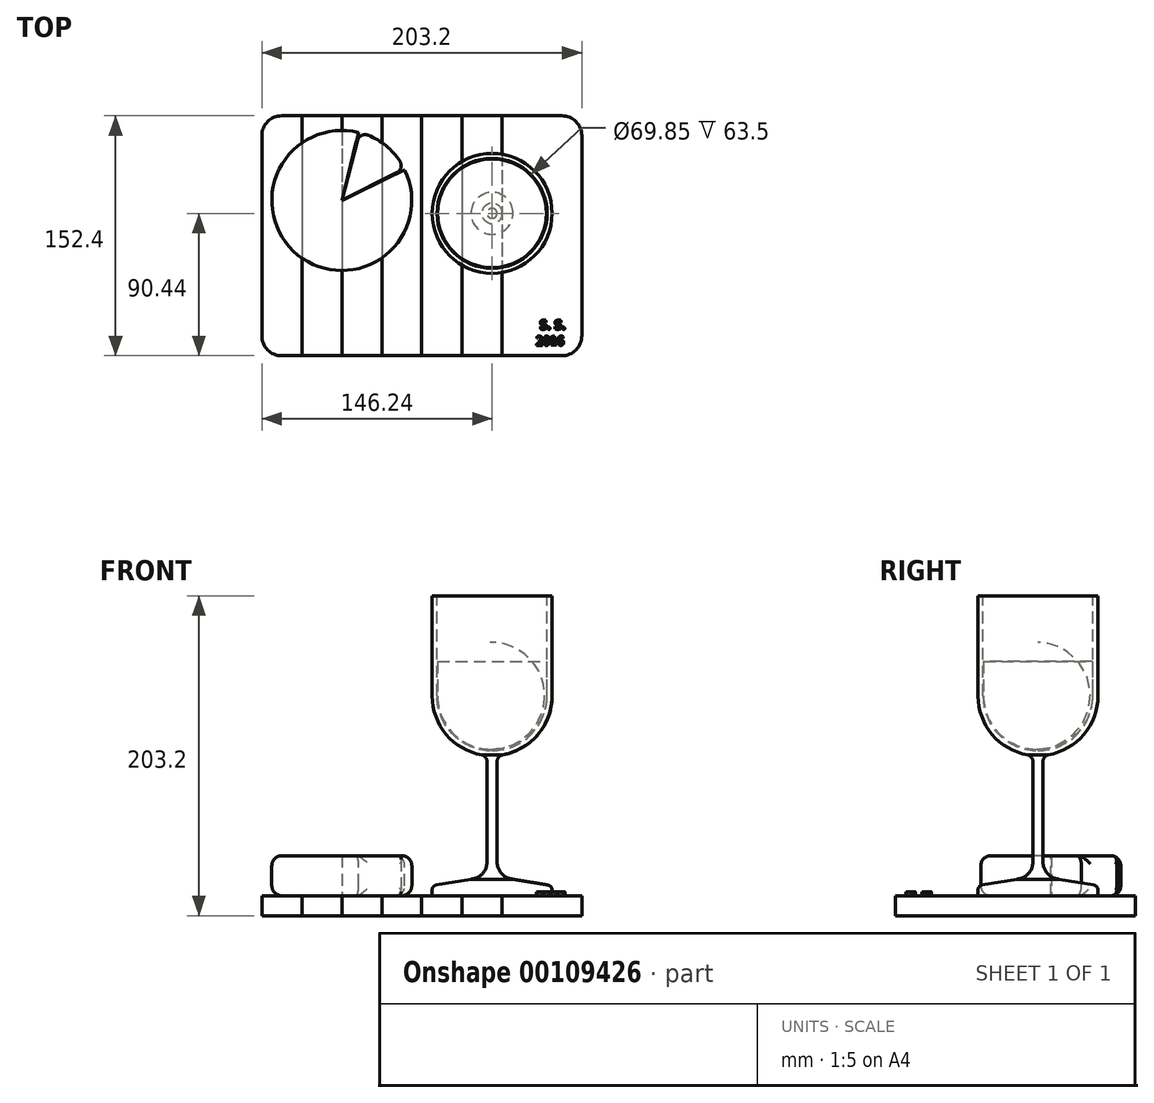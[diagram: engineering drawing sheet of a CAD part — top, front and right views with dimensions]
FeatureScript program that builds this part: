
annotation { "Feature Type Name" : "Feature", "Feature Type Description" : "" }
export const myFeature = defineFeature(function(context is Context, id is Id, definition is map)
    precondition{}
    {
        {
            var Q0;
            Q0=qCreatedBy(makeId("Front.planeOp"),FACE);
            var sketch = newSketch(context, id + "F0", { "sketchPlane" : qUnion([Q0])});
            skLineSegment(sketch, "E0", {"start": v(0, 209.71) * mm, "end": v(0, -15.34) * mm, "construction": true});
            skLineSegment(sketch, "E1", {"start": v(0, 0) * mm, "end": v(-38.1, 0) * mm});
            skLineSegment(sketch, "E2", {"start": v(-38.1, 0) * mm, "end": v(-38.1, 3.66) * mm});
            skLineSegment(sketch, "E3", {"start": v(-35.45, 6.8) * mm, "end": v(-13.34, 10.48) * mm});
            skLineSegment(sketch, "E4", {"start": v(0, 12.7) * mm, "end": v(0, 0) * mm});
            skLineSegment(sketch, "E5", {"start": v(-38.1, 190.5) * mm, "end": v(-38.1, 127) * mm});
            skArc(sketch, "E6", {"start": v(-38.1, 127) * mm, "mid": v(-29.14, 102.46) * mm, "end": v(-6.48, 89.46) * mm});
            skPoint(sketch, "E7.visualSharp", {"position": v(-38.1, 6.35) * mm});
            skArc(sketch, "E7.filletArc", {"start": v(-35.45, 6.8) * mm, "mid": v(-37.35, 5.71) * mm, "end": v(-38.1, 3.66) * mm});
            skArc(sketch, "E8.0", {"start": v(-34.92, 127) * mm, "mid": v(-24.7, 102.3) * mm, "end": v(0, 92.07) * mm});
            skLineSegment(sketch, "E8.1", {"start": v(-34.92, 190.5) * mm, "end": v(-34.92, 127) * mm});
            skLineSegment(sketch, "E9", {"start": v(-38.1, 190.5) * mm, "end": v(-34.92, 190.5) * mm});
            skLineSegment(sketch, "E10", {"start": v(0, 88.9) * mm, "end": v(0, 92.07) * mm});
            skLineSegment(sketch, "E11", {"start": v(0, 12.7) * mm, "end": v(0, 88.9) * mm});
            skLineSegment(sketch, "E12", {"start": v(-3.17, 85.1) * mm, "end": v(-3.17, 21.6) * mm});
            skArc(sketch, "E13", {"start": v(-3.17, 85.1) * mm, "mid": v(-4.1, 87.83) * mm, "end": v(-6.48, 89.46) * mm});
            skArc(sketch, "E14", {"start": v(-3.17, 21.6) * mm, "mid": v(-6.1, 14.06) * mm, "end": v(-13.34, 10.48) * mm});
            skSolve(sketch);
        }
        {
            var Q0;
            Q0 = qSketchRegion(id + "F0", true);
            var Q1;
            Q1=sQuery(id+"F0.wireOp",EDGE,"E0");
            revolve(context, id + "F1", {"entities" : qUnion([Q0]), "axis" : qUnion([Q1]), "revolveType" : RevolveType.FULL});
        }
        {
            var Q0;
            Q0=qCreatedBy(makeId("Front.planeOp"),FACE);
            var sketch = newSketch(context, id + "F2", { "sketchPlane" : qUnion([Q0])});
            skLineSegment(sketch, "E15", {"start": v(0, 148.84) * mm, "end": v(0, 93.04) * mm});
            skLineSegment(sketch, "E16", {"start": v(0, 148.84) * mm, "end": v(-34.57, 148.84) * mm});
            skLineSegment(sketch, "E17", {"start": v(-34.57, 148.84) * mm, "end": v(-34.57, 126.99) * mm});
            skArc(sketch, "E18", {"start": v(-34.57, 126.99) * mm, "mid": v(-24.4, 102.76) * mm, "end": v(0, 93.04) * mm});
            skSolve(sketch);
        }
        {
            var Q0;
            Q0 = qSketchRegion(id + "F2", true);
            var Q1;
            Q1=sQuery(id+"F0.wireOp",EDGE,"E11");
            revolve(context, id + "F3", {"entities" : qUnion([Q0]), "axis" : qUnion([Q1]), "revolveType" : RevolveType.FULL});
        }
        {
            var Q0;
            Q0=qCreatedBy(makeId("Top.planeOp"),FACE);
            var sketch = newSketch(context, id + "F4", { "sketchPlane" : qUnion([Q0])});
            skLineSegment(sketch, "E19.bottom", {"start": v(44.26, 61.96) * mm, "end": v(-133.54, 61.96) * mm});
            skLineSegment(sketch, "E19.top", {"start": v(44.26, -90.44) * mm, "end": v(-133.54, -90.44) * mm});
            skLineSegment(sketch, "E19.left", {"start": v(56.96, 49.26) * mm, "end": v(56.96, -77.74) * mm});
            skLineSegment(sketch, "E19.right", {"start": v(-146.24, 49.26) * mm, "end": v(-146.24, -77.74) * mm});
            skPoint(sketch, "E19.middle", {"position": v(-44.64, -14.24) * mm});
            skPoint(sketch, "E20.visualSharp", {"position": v(-146.24, 61.96) * mm});
            skArc(sketch, "E20.filletArc", {"start": v(-133.54, 61.96) * mm, "mid": v(-142.52, 58.24) * mm, "end": v(-146.24, 49.26) * mm});
            skPoint(sketch, "E21.visualSharp", {"position": v(-146.24, -90.44) * mm});
            skArc(sketch, "E21.filletArc", {"start": v(-146.24, -77.74) * mm, "mid": v(-142.52, -86.72) * mm, "end": v(-133.54, -90.44) * mm});
            skPoint(sketch, "E22.visualSharp", {"position": v(56.96, -90.44) * mm});
            skArc(sketch, "E22.filletArc", {"start": v(44.26, -90.44) * mm, "mid": v(53.24, -86.72) * mm, "end": v(56.96, -77.74) * mm});
            skPoint(sketch, "E23.visualSharp", {"position": v(56.96, 61.96) * mm});
            skArc(sketch, "E23.filletArc", {"start": v(56.96, 49.26) * mm, "mid": v(53.24, 58.24) * mm, "end": v(44.26, 61.96) * mm});
            skLineSegment(sketch, "E24", {"start": v(-120.84, 61.96) * mm, "end": v(-120.84, -90.44) * mm});
            skLineSegment(sketch, "E25", {"start": v(-70.04, 61.96) * mm, "end": v(-70.04, -90.44) * mm});
            skLineSegment(sketch, "E26", {"start": v(-44.64, 61.96) * mm, "end": v(-44.64, -90.44) * mm});
            skLineSegment(sketch, "E27", {"start": v(-19.24, 61.96) * mm, "end": v(-19.24, -90.44) * mm});
            skLineSegment(sketch, "E28", {"start": v(31.56, 61.96) * mm, "end": v(31.56, -90.44) * mm});
            skLineSegment(sketch, "E29", {"start": v(-95.44, 61.96) * mm, "end": v(-95.44, -90.44) * mm});
            skLineSegment(sketch, "E30", {"start": v(6.16, 61.96) * mm, "end": v(6.16, -90.44) * mm});
            skSolve(sketch);
        }
        {
            var Q0;
            Q0=makeQuery(id+"F4.imprint","IMPRINT",FACE,{"disambiguationData":[TD([[makeQuery(id+"F4.imprint","IMPRINT",EDGE,{"derivedFrom":sQuery(id+"F4.wireOp",EDGE,"E19.right")}),1.0]])]});
            var Q1;
            {var subQ0=sQuery(id+"F4.wireOp",EDGE,"E25");Q1=makeQuery(id+"F4.imprint","IMPRINT",FACE,{"disambiguationData":[TD([[makeQuery(id+"F4.imprint","IMPRINT",EDGE,{"derivedFrom":subQ0}),-1.0]])]});}
            var Q2;
            {var subQ0=sQuery(id+"F4.wireOp",EDGE,"E26");Q2=makeQuery(id+"F4.imprint","IMPRINT",FACE,{"disambiguationData":[TD([[makeQuery(id+"F4.imprint","IMPRINT",EDGE,{"derivedFrom":subQ0}),1.0]])]});}
            var Q3;
            {var subQ0=sQuery(id+"F4.wireOp",EDGE,"E28");Q3=makeQuery(id+"F4.imprint","IMPRINT",FACE,{"disambiguationData":[TD([[makeQuery(id+"F4.imprint","IMPRINT",EDGE,{"derivedFrom":subQ0}),-1.0]])]});}
            extrude(context, id + "F5", {"entities" : qUnion([Q0, Q1, Q2, Q3]), "oppositeDirection" : true, "depth" : 12.7 * mm});
        }
        {
            var Q0;
            {var subQ0=sQuery(id+"F4.wireOp",EDGE,"E24");Q0=makeQuery(id+"F4.imprint","IMPRINT",FACE,{"disambiguationData":[TD([[makeQuery(id+"F4.imprint","IMPRINT",EDGE,{"derivedFrom":subQ0}),1.0]])]});}
            var Q1;
            {var subQ0=sQuery(id+"F4.wireOp",EDGE,"E25");Q1=makeQuery(id+"F4.imprint","IMPRINT",FACE,{"disambiguationData":[TD([[makeQuery(id+"F4.imprint","IMPRINT",EDGE,{"derivedFrom":subQ0}),1.0]])]});}
            var Q2;
            {var subQ0=sQuery(id+"F4.wireOp",EDGE,"E27");Q2=makeQuery(id+"F4.imprint","IMPRINT",FACE,{"disambiguationData":[TD([[makeQuery(id+"F4.imprint","IMPRINT",EDGE,{"derivedFrom":subQ0}),1.0]])]});}
            var Q3;
            Q3=makeQuery(id+"F4.imprint","IMPRINT",FACE,{"disambiguationData":[TD([[makeQuery(id+"F4.imprint","IMPRINT",EDGE,{"derivedFrom":sQuery(id+"F4.wireOp",EDGE,"E19.left")}),-1.0]])]});
            extrude(context, id + "F6", {"entities" : qUnion([Q0, Q1, Q2, Q3]), "oppositeDirection" : true, "depth" : 12.7 * mm});
        }
        {
            var Q0;
            Q0=makeQuery(id+"F6.opExtrude","CAP_FACE",FACE,{"disambiguationData":[OSD([sQuery(id+"F4.wireOp",EDGE,"E19.bottom"),sQuery(id+"F4.wireOp",EDGE,"E19.top"),sQuery(id+"F4.wireOp",EDGE,"E24"),sQuery(id+"F4.wireOp",EDGE,"E29")])],"isStart":true});
            var sketch = newSketch(context, id + "F7", { "sketchPlane" : qUnion([Q0])});
            skCircle(sketch, "E31", {"center": v(-95.44, 8.16) * mm, "radius": 44.45 * mm});
            skSolve(sketch);
        }
        {
            var Q0;
            Q0 = qSketchRegion(id + "F7", true);
            extrude(context, id + "F8", {"entities" : qUnion([Q0]), "depth" : 25.4 * mm});
        }
        {
            var Q0;
            Q0=makeQuery(id+"F8.opExtrude","CAP_FACE",FACE,{"disambiguationData":[OSD([sQuery(id+"F7.wireOp",EDGE,"E31")])],"isStart":false});
            var Q1;
            Q1=makeQuery(id+"F8.opExtrude","SWEPT_FACE",FACE,{"disambiguationData":[OSD([sQuery(id+"F7.wireOp",EDGE,"E31")])]});
            fillet(context, id + "F9", {"entities" : qUnion([Q0, Q1]), "radius" : 6.35 * mm, "tangentPropagation" : true, "allowEdgeOverflow" : false});
        }
        {
            var Q0;
            Q0=makeQuery(id+"F8.opExtrude","CAP_FACE",FACE,{"disambiguationData":[OSD([sQuery(id+"F7.wireOp",EDGE,"E31")])],"isStart":false});
            var sketch = newSketch(context, id + "F10", { "sketchPlane" : qUnion([Q0])});
            skLineSegment(sketch, "E32", {"start": v(-95.44, 8.16) * mm, "end": v(-84.76, 51.3) * mm});
            skLineSegment(sketch, "E33", {"start": v(-95.44, 8.16) * mm, "end": v(-55.46, 27.6) * mm});
            skArc(sketch, "E34", {"start": v(-55.46, 27.6) * mm, "mid": v(-51.47, 62.48) * mm, "end": v(-84.76, 51.3) * mm});
            skSolve(sketch);
        }
        {
            var Q0;
            Q0 = qSketchRegion(id + "F10", true);
            extrude(context, id + "F11", {"entities" : qUnion([Q0]), "operationType" : NewBodyOperationType.REMOVE, "oppositeDirection" : true, "depth" : 25.4 * mm});
        }
        {
            var Q0;
            Q0=makeQuery(id+"F5.opExtrude","CAP_FACE",FACE,{"disambiguationData":[OSD([sQuery(id+"F4.wireOp",EDGE,"E19.bottom"),sQuery(id+"F4.wireOp",EDGE,"E19.top"),sQuery(id+"F4.wireOp",EDGE,"E25"),sQuery(id+"F4.wireOp",EDGE,"E29")])],"isStart":true});
            var sketch = newSketch(context, id + "F12", { "sketchPlane" : qUnion([Q0])});
            skLineSegment(sketch, "E35", {"start": v(-95.44, 8.55) * mm, "end": v(-84.12, 51.44) * mm});
            skLineSegment(sketch, "E36", {"start": v(-95.44, 8.55) * mm, "end": v(-55.68, 28.2) * mm});
            skArc(sketch, "E37", {"start": v(-55.68, 28.2) * mm, "mid": v(-67.38, 42.9) * mm, "end": v(-84.12, 51.44) * mm});
            skSolve(sketch);
        }
        {
            var Q0;
            Q0 = qSketchRegion(id + "F12", true);
            extrude(context, id + "F13", {"entities" : qUnion([Q0]), "depth" : 25.4 * mm});
        }
        {
            var Q0;
            Q0=makeQuery(id+"F13.opExtrude","SWEPT_FACE",FACE,{"disambiguationData":[OSD([sQuery(id+"F12.wireOp",EDGE,"E37")])]});
            fillet(context, id + "F14", {"entities" : qUnion([Q0]), "radius" : 5.08 * mm, "tangentPropagation" : true, "allowEdgeOverflow" : false});
        }
        {
            var Q0;
            Q0=makeQuery(id+"F6.opExtrude","CAP_FACE",FACE,{"disambiguationData":[OSD([sQuery(id+"F4.wireOp",EDGE,"E19.bottom"),sQuery(id+"F4.wireOp",EDGE,"E19.top"),sQuery(id+"F4.wireOp",EDGE,"E19.left"),sQuery(id+"F4.wireOp",EDGE,"E22.filletArc"),sQuery(id+"F4.wireOp",EDGE,"E23.filletArc"),sQuery(id+"F4.wireOp",EDGE,"E28")])],"isStart":true});
            var sketch = newSketch(context, id + "F15", { "sketchPlane" : qUnion([Q0])});
            skText(sketch, "E38", { "text": " S. S.\n2016", "fontName": "Tinos-Bold.ttf"});
            const initialGuessF15  = {"E38": [0.02797, -0.07368, 1, 0.00206, 0.00635]};
            skSetInitialGuess(sketch, initialGuessF15);
            skSolve(sketch);
        }
        {
            var Q0;
            Q0 = qSketchRegion(id + "F15", true);
            extrude(context, id + "F16", {"entities" : qUnion([Q0]), "operationType" : NewBodyOperationType.ADD, "depth" : 2.54 * mm});
        }
    });
